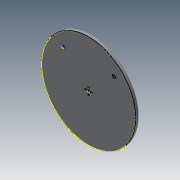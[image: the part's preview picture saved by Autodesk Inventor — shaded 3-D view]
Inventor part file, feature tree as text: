
AUTODESK INVENTOR PART (.ipt)
format: ipt  version: 2015 (Build 190159000, 159)  size: 105,472 bytes
history: native  units: mm
features: other x6, sketch x2, plane x1, extrude x1, projected_geometry x1
ambient origin geometry x8: Origin, YZ Plane, XZ Plane, XY Plane, X Axis, Y Axis, Z Axis, Center Point
bodies: Body1 (feature_tree)
feature tree (11):
  other  "Blocks"
  sketch  "Sketch1"  dims[d0=300.0mm d1=10.0mm]
  plane  "Work Plane1"
  extrude  "Extrusion4"  Depth=10.0mm
  sketch  "Sketch4"  dims[d2=10.0mm d7=105.0mm d8=40.0mm d9=4.0mm d10=40.0mm d12=360.0deg d18=10.0mm d26=10.0mm d27=0.0mm]
  other  "DXF"
  other  "Block1"
  projected_geometry  "Projected Loop1"
  other  "Block2"
  other  "Block2:1"
  other  "Block2:2"
